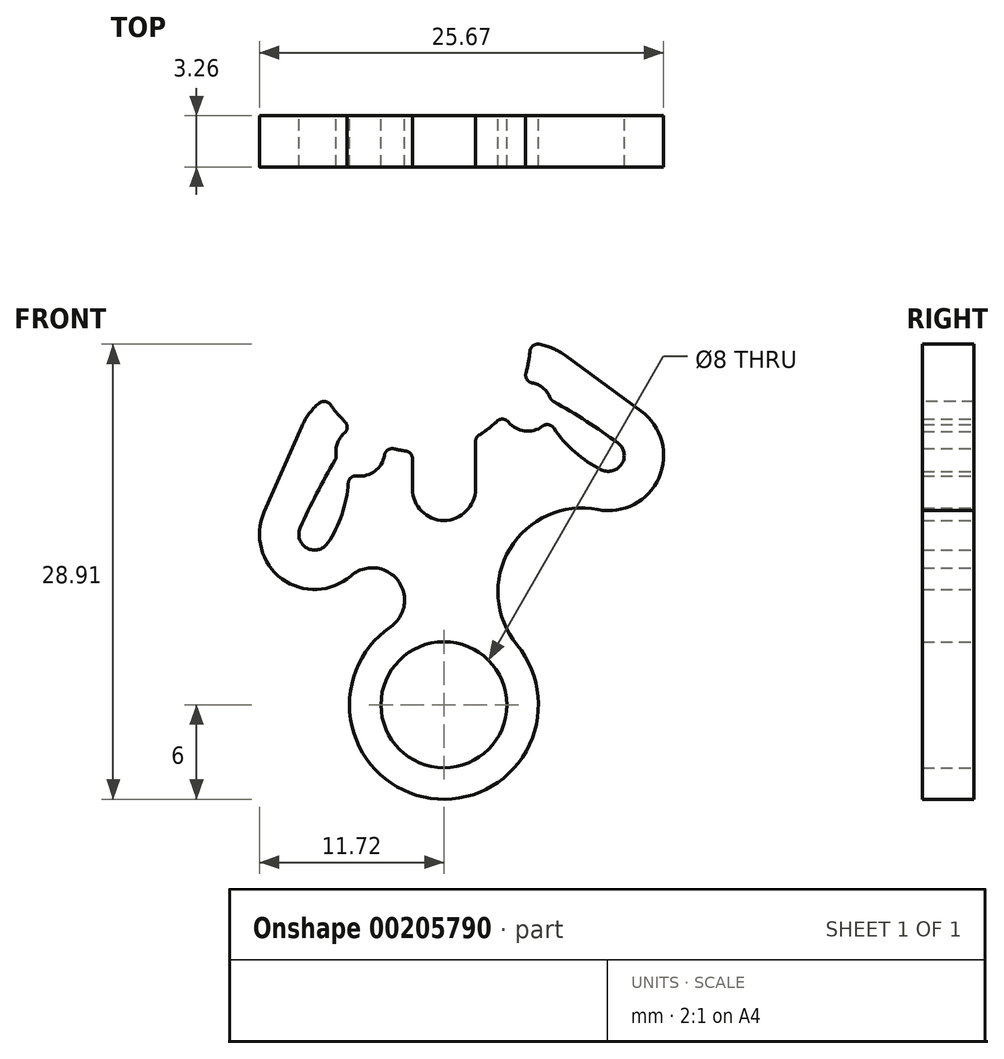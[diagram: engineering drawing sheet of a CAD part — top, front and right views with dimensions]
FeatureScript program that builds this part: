
annotation { "Feature Type Name" : "Feature", "Feature Type Description" : "" }
export const myFeature = defineFeature(function(context is Context, id is Id, definition is map)
    precondition{}
    {
        {
            var Q0;
            Q0=qCreatedBy(makeId("Front.planeOp"),FACE);
            var sketch = newSketch(context, id + "F0", { "sketchPlane" : qUnion([Q0])});
            skCircle(sketch, "E0", {"center": v(0, 0) * mm, "radius": 4 * mm});
            skCircle(sketch, "E1", {"center": v(0, 0) * mm, "radius": 6 * mm});
            skLineSegment(sketch, "E2", {"start": v(0, 0) * mm, "end": v(0, 17.5) * mm, "construction": true});
            skLineSegment(sketch, "E3", {"start": v(-5.31, 16.08) * mm, "end": v(5.31, 18.92) * mm, "construction": true});
            skCircle(sketch, "E4", {"center": v(-5.31, 16.08) * mm, "radius": 1.55 * mm});
            skCircle(sketch, "E5", {"center": v(5.31, 18.92) * mm, "radius": 1.55 * mm});
            skCircle(sketch, "E6", {"center": v(-1.48, 23.01) * mm, "radius": 6.38 * mm, "construction": true});
            skPoint(sketch, "E7", {"position": v(-4.56, 17.43) * mm});
            skPoint(sketch, "E8", {"position": v(3.98, 19.72) * mm});
            skSolve(sketch);
        }
        {
            var Q0;
            Q0=qCreatedBy(makeId("Front.planeOp"),FACE);
            var sketch = newSketch(context, id + "F1", { "sketchPlane" : qUnion([Q0])});
            skPoint(sketch, "E9.0", {"position": v(-5.31, 16.08) * mm});
            skPoint(sketch, "E10.0", {"position": v(5.31, 18.92) * mm});
            skPoint(sketch, "E11.0", {"position": v(0, 0) * mm});
            skPoint(sketch, "E12.0", {"position": v(-1.48, 23.01) * mm});
            skCircle(sketch, "E13.0", {"center": v(-1.48, 23.01) * mm, "radius": 6.38 * mm, "construction": true});
            skLineSegment(sketch, "E14", {"start": v(-1.48, 23.01) * mm, "end": v(-8.22, 10.83) * mm, "construction": true});
            skArc(sketch, "E15", {"start": v(-11.42, 12.24) * mm, "mid": v(-10.29, 8) * mm, "end": v(-5.91, 8.2) * mm});
            skLineSegment(sketch, "E16", {"start": v(-11.42, 12.24) * mm, "end": v(-9.01, 17.7) * mm});
            skArc(sketch, "E17", {"start": v(-9.13, 11.23) * mm, "mid": v(-8.7, 9.95) * mm, "end": v(-7.39, 10.26) * mm});
            skLineSegment(sketch, "E18", {"start": v(-9.13, 11.23) * mm, "end": v(-6.67, 16.83) * mm, "construction": true});
            skLineSegment(sketch, "E19", {"start": v(-7.39, 10.26) * mm, "end": v(-3.96, 15.33) * mm, "construction": true});
            skArc(sketch, "E20", {"start": v(-3.4, 4.95) * mm, "mid": v(-2.93, 7.9) * mm, "end": v(-5.91, 8.2) * mm});
            skArc(sketch, "E21.0", {"start": v(-3.4, 4.95) * mm, "mid": v(-5.73, -1.78) * mm, "end": v(0, -6) * mm});
            skArc(sketch, "E22.0", {"start": v(0, 4) * mm, "mid": v(-4, 0) * mm, "end": v(0, -4) * mm});
            skPoint(sketch, "E23", {"position": v(-2.5, 6.64) * mm});
            skArc(sketch, "E24.trimOffspring", {"start": v(-7.48, 19.49) * mm, "mid": v(-8.38, 18.71) * mm, "end": v(-9.01, 17.7) * mm});
            skArc(sketch, "E25", {"start": v(-7.48, 19.49) * mm, "mid": v(-6.73, 18.44) * mm, "end": v(-5.8, 17.55) * mm});
            skLineSegment(sketch, "E26", {"start": v(0, 11.7) * mm, "end": v(0, 4) * mm, "construction": true});
            skArc(sketch, "E27.trimOffspring", {"start": v(-3.8, 16.45) * mm, "mid": v(-2.92, 16.2) * mm, "end": v(-2, 16.07) * mm});
            skLineSegment(sketch, "E28", {"start": v(0, -4) * mm, "end": v(0, -6) * mm, "construction": true});
            skPoint(sketch, "E29.orphan", {"position": v(0, 16.8) * mm});
            skLineSegment(sketch, "E30", {"start": v(-6.67, 16.83) * mm, "end": v(-3.96, 15.33) * mm, "construction": true});
            skArc(sketch, "E31", {"start": v(-5.8, 17.55) * mm, "mid": v(-6.3, 17.27) * mm, "end": v(-6.67, 16.83) * mm});
            skArc(sketch, "E32.MirrorCS", {"start": v(-3.8, 16.45) * mm, "mid": v(-3.78, 15.88) * mm, "end": v(-3.96, 15.33) * mm});
            skArc(sketch, "E33.MirrorCS", {"start": v(-6.82, 15.7) * mm, "mid": v(-6.85, 16.28) * mm, "end": v(-6.67, 16.83) * mm});
            skArc(sketch, "E34.MirrorCS", {"start": v(-6.06, 14.72) * mm, "mid": v(-4.88, 14.59) * mm, "end": v(-3.96, 15.33) * mm});
            skArc(sketch, "E35", {"start": v(-6.82, 15.7) * mm, "mid": v(-8.04, 13.5) * mm, "end": v(-9.13, 11.23) * mm});
            skArc(sketch, "E36", {"start": v(-7.39, 10.26) * mm, "mid": v(-6.38, 12.4) * mm, "end": v(-6.06, 14.72) * mm});
            skLineSegment(sketch, "E37", {"start": v(-2, 13.7) * mm, "end": v(-2, 16.07) * mm});
            skPoint(sketch, "E37.startSnap0", {"position": v(-2, 16.07) * mm});
            skArc(sketch, "E38", {"start": v(-2, 13.7) * mm, "mid": v(-1.41, 12.3) * mm, "end": v(0, 11.7) * mm});
            skPoint(sketch, "E39.orphan", {"position": v(0, 16.2) * mm});
            skArc(sketch, "E40.0", {"start": v(3.82, 18.5) * mm, "mid": v(5.1, 17.39) * mm, "end": v(6.64, 18.12) * mm});
            skLineSegment(sketch, "E41.MirrorCS", {"start": v(2, 13.7) * mm, "end": v(2, 16.98) * mm});
            skArc(sketch, "E42.MirrorCS", {"start": v(2, 13.7) * mm, "mid": v(1.41, 12.3) * mm, "end": v(0, 11.7) * mm});
            skArc(sketch, "E43.MirrorCS", {"start": v(4.64, 3.8) * mm, "mid": v(5.42, -2.56) * mm, "end": v(0, -6) * mm});
            skArc(sketch, "E44.MirrorCS", {"start": v(0, 4) * mm, "mid": v(4, 0) * mm, "end": v(0, -4) * mm});
            skLineSegment(sketch, "E45", {"start": v(-1.48, 23.01) * mm, "end": v(10.45, 15.83) * mm, "construction": true});
            skCircle(sketch, "E46", {"center": v(-1.48, 23.01) * mm, "radius": 7.93 * mm, "construction": true});
            skLineSegment(sketch, "E47", {"start": v(-1.48, 23.01) * mm, "end": v(0.57, 15.36) * mm, "construction": true});
            skLineSegment(sketch, "E48", {"start": v(-5.31, 16.08) * mm, "end": v(5.31, 18.92) * mm, "construction": true});
            skPoint(sketch, "E49", {"position": v(0, 17.5) * mm});
            skArc(sketch, "E50.MirrorCS", {"start": v(11.04, 16.64) * mm, "mid": v(11.3, 15.31) * mm, "end": v(10.02, 14.93) * mm});
            skArc(sketch, "E51.MirrorCS", {"start": v(6.8, 19.35) * mm, "mid": v(8.97, 18.06) * mm, "end": v(11.04, 16.64) * mm});
            skArc(sketch, "E52.MirrorCS", {"start": v(10.02, 14.93) * mm, "mid": v(8.08, 16.27) * mm, "end": v(6.64, 18.12) * mm});
            skArc(sketch, "E53.MirrorCS", {"start": v(12.52, 18.65) * mm, "mid": v(13.66, 14.42) * mm, "end": v(9.77, 12.4) * mm});
            skLineSegment(sketch, "E54.MirrorCS", {"start": v(12.52, 18.65) * mm, "end": v(7.7, 22.18) * mm});
            skArc(sketch, "E55.MirrorCS", {"start": v(3.82, 18.5) * mm, "mid": v(2.98, 17.66) * mm, "end": v(2, 16.98) * mm});
            skArc(sketch, "E56.MirrorCS", {"start": v(5.48, 22.96) * mm, "mid": v(5.35, 21.68) * mm, "end": v(5, 20.44) * mm});
            skArc(sketch, "E57", {"start": v(9.77, 12.4) * mm, "mid": v(4.18, 9.91) * mm, "end": v(4.64, 3.8) * mm});
            skArc(sketch, "E58.trimOffspring", {"start": v(7.7, 22.18) * mm, "mid": v(6.65, 22.74) * mm, "end": v(5.48, 22.96) * mm});
            skArc(sketch, "E59.trimOffspring", {"start": v(6.8, 19.35) * mm, "mid": v(6.11, 20.25) * mm, "end": v(5, 20.44) * mm});
            skSolve(sketch);
        }
        {
            var Q0;
            Q0 = qSketchRegion(id + "F1", true);
            extrude(context, id + "F2", {"entities" : qUnion([Q0]), "depth" : 3.25 * mm, "symmetric" : true});
        }
        {
            var Q0;
            Q0=makeQuery(id+"F2.opExtrude","SWEPT_EDGE",EDGE,{"disambiguationData":[OSD([sQuery(id+"F1.wireOp",EDGE,"1e8f439e-6b3d-448d-9ed5-9f96a4d8027d.0"),sQuery(id+"F1.wireOp",EDGE,"E27.trimOffspring")])]});
            var Q1;
            Q1=makeQuery(id+"F2.opExtrude","SWEPT_EDGE",EDGE,{"disambiguationData":[OSD([sQuery(id+"F1.wireOp",EDGE,"a0f55a07-d862-4c9f-a472-f0dc4c802180.trimOffspring"),sQuery(id+"F1.wireOp",EDGE,"E25")])]});
            var Q2;
            Q2=makeQuery(id+"F2.opExtrude","SWEPT_EDGE",EDGE,{"disambiguationData":[OSD([sQuery(id+"F1.wireOp",EDGE,"E24.trimOffspring"),sQuery(id+"F1.wireOp",EDGE,"E25")])]});
            var Q3;
            Q3=makeQuery(id+"F2.opExtrude","SWEPT_EDGE",EDGE,{"disambiguationData":[OSD([sQuery(id+"F1.wireOp",EDGE,"E33.MirrorCS"),sQuery(id+"F1.wireOp",EDGE,"E35")])]});
            var Q4;
            Q4=makeQuery(id+"F2.opExtrude","SWEPT_EDGE",EDGE,{"disambiguationData":[OSD([sQuery(id+"F1.wireOp",EDGE,"E34.MirrorCS"),sQuery(id+"F1.wireOp",EDGE,"E36")])]});
            var Q5;
            Q5=makeQuery(id+"F2.opExtrude","SWEPT_EDGE",EDGE,{"disambiguationData":[OSD([sQuery(id+"F1.wireOp",EDGE,"E41.MirrorCS"),sQuery(id+"F1.wireOp",EDGE,"E55.MirrorCS")])]});
            var Q6;
            Q6=makeQuery(id+"F2.opExtrude","SWEPT_EDGE",EDGE,{"disambiguationData":[OSD([sQuery(id+"F1.wireOp",EDGE,"E40.0"),sQuery(id+"F1.wireOp",EDGE,"E55.MirrorCS")])]});
            var Q7;
            Q7=makeQuery(id+"F2.opExtrude","SWEPT_EDGE",EDGE,{"disambiguationData":[OSD([sQuery(id+"F1.wireOp",EDGE,"E40.0"),sQuery(id+"F1.wireOp",EDGE,"E52.MirrorCS")])]});
            var Q8;
            Q8=makeQuery(id+"F2.opExtrude","SWEPT_EDGE",EDGE,{"disambiguationData":[OSD([sQuery(id+"F1.wireOp",EDGE,"E56.MirrorCS"),sQuery(id+"F1.wireOp",EDGE,"E59.trimOffspring")])]});
            var Q9;
            Q9=makeQuery(id+"F2.opExtrude","SWEPT_EDGE",EDGE,{"disambiguationData":[OSD([sQuery(id+"F1.wireOp",EDGE,"E51.MirrorCS"),sQuery(id+"F1.wireOp",EDGE,"E59.trimOffspring")])]});
            var Q10;
            Q10=makeQuery(id+"F2.opExtrude","SWEPT_EDGE",EDGE,{"disambiguationData":[OSD([sQuery(id+"F1.wireOp",EDGE,"E56.MirrorCS"),sQuery(id+"F1.wireOp",EDGE,"E58.trimOffspring")])]});
            fillet(context, id + "F3", {"entities" : qUnion([Q0, Q1, Q2, Q3, Q4, Q5, Q6, Q7, Q8, Q9, Q10]), "radius" : 0.5 * mm, "tangentPropagation" : true, "allowEdgeOverflow" : false});
        }
    });
